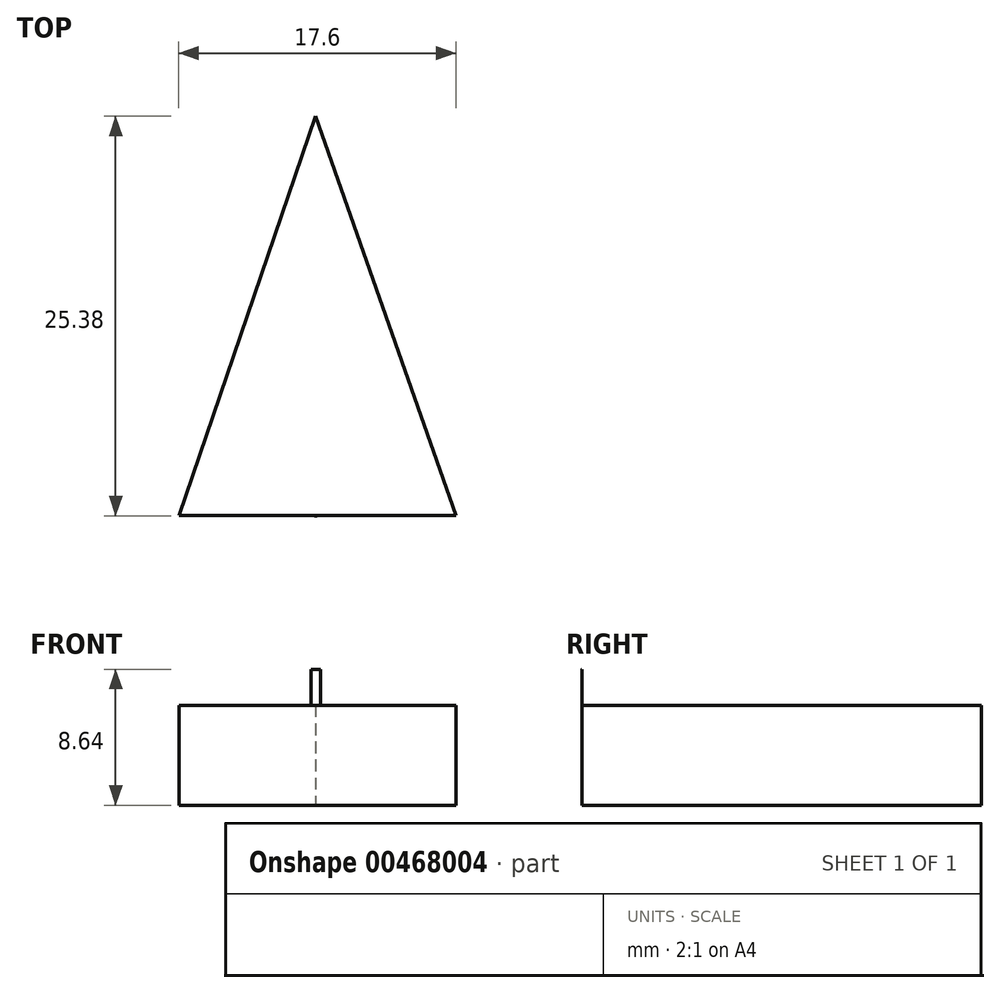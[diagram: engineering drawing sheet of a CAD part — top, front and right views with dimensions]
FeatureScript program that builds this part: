
annotation { "Feature Type Name" : "Feature", "Feature Type Description" : "" }
export const myFeature = defineFeature(function(context is Context, id is Id, definition is map)
    precondition{}
    {
        {
            var Q0;
            Q0=qCreatedBy(makeId("Top.planeOp"),FACE);
            var sketch = newSketch(context, id + "F0", { "sketchPlane" : qUnion([Q0])});
            skLineSegment(sketch, "E0", {"start": v(0, 0) * mm, "end": v(0, 25.37) * mm});
            skLineSegment(sketch, "E1", {"start": v(0, 25.37) * mm, "end": v(8.9, 0) * mm});
            skLineSegment(sketch, "E2", {"start": v(8.9, 0) * mm, "end": v(0, 25.37) * mm});
            skLineSegment(sketch, "E3", {"start": v(0, 25.37) * mm, "end": v(-8.7, 0) * mm});
            skLineSegment(sketch, "E4", {"start": v(-8.7, 0) * mm, "end": v(8.9, 0) * mm});
            skSolve(sketch);
        }
        {
            var Q0;
            Q0 = qSketchRegion(id + "F0", true);
            extrude(context, id + "F1", {"entities" : qUnion([Q0]), "depth" : 6.35 * mm});
        }
        {
            var Q0;
            Q0=makeQuery(id+"F1.opExtrude","CAP_FACE",FACE,{"disambiguationData":[OSD([sQuery(id+"F0.wireOp",EDGE,"E2"),sQuery(id+"F0.wireOp",EDGE,"E3"),sQuery(id+"F0.wireOp",EDGE,"E4")])],"isStart":false});
            var sketch = newSketch(context, id + "F2", { "sketchPlane" : qUnion([Q0])});
            skLineSegment(sketch, "E5", {"start": v(0, 25.37) * mm, "end": v(0, 0) * mm});
            skLineSegment(sketch, "E6", {"start": v(0, 0) * mm, "end": v(0, 25.37) * mm});
            skCircle(sketch, "E7", {"center": v(0, 6.14) * mm, "radius": 6.15 * mm});
            skSolve(sketch);
        }
        {
            var Q0;
            {var subQ0=sQuery(id+"F2.wireOp",EDGE,"E6");var subQ1=makeQuery(id+"F1.opExtrude","CAP_EDGE",EDGE,{"disambiguationData":[OSD([sQuery(id+"F0.wireOp",EDGE,"E4")])],"isStart":false});var subQ2=makeQuery(id+"F2.imprint","INTERSECT",VERTEX,{"derivedFrom":[subQ1,subQ0]});Q0=makeQuery(id+"F2.imprint","IMPRINT",FACE,{"disambiguationData":[TD([[makeQuery(id+"F2.imprint","IMPRINT",EDGE,{"disambiguationData":[TD([[subQ2,-1.0]])],"derivedFrom":subQ0}),-1.0]])]});}
            var Q1;
            {var subQ0=sQuery(id+"F2.wireOp",EDGE,"E7");var subQ1=makeQuery(id+"F1.opExtrude","CAP_EDGE",EDGE,{"disambiguationData":[OSD([sQuery(id+"F0.wireOp",EDGE,"E4")])],"isStart":false});var subQ2=makeQuery(id+"F2.imprint","INTERSECT",VERTEX,{"disambiguationData":[OD(0.0)],"derivedFrom":[subQ1,subQ0]});Q1=makeQuery(id+"F2.imprint","IMPRINT",FACE,{"disambiguationData":[TD([[makeQuery(id+"F2.imprint","IMPRINT",EDGE,{"disambiguationData":[TD([[subQ2,-1.0]])],"derivedFrom":subQ0}),1.0]])]});}
            extrude(context, id + "F3", {"entities" : qUnion([Q0, Q1]), "operationType" : NewBodyOperationType.ADD, "depth" : 2.3 * mm});
        }
    });
